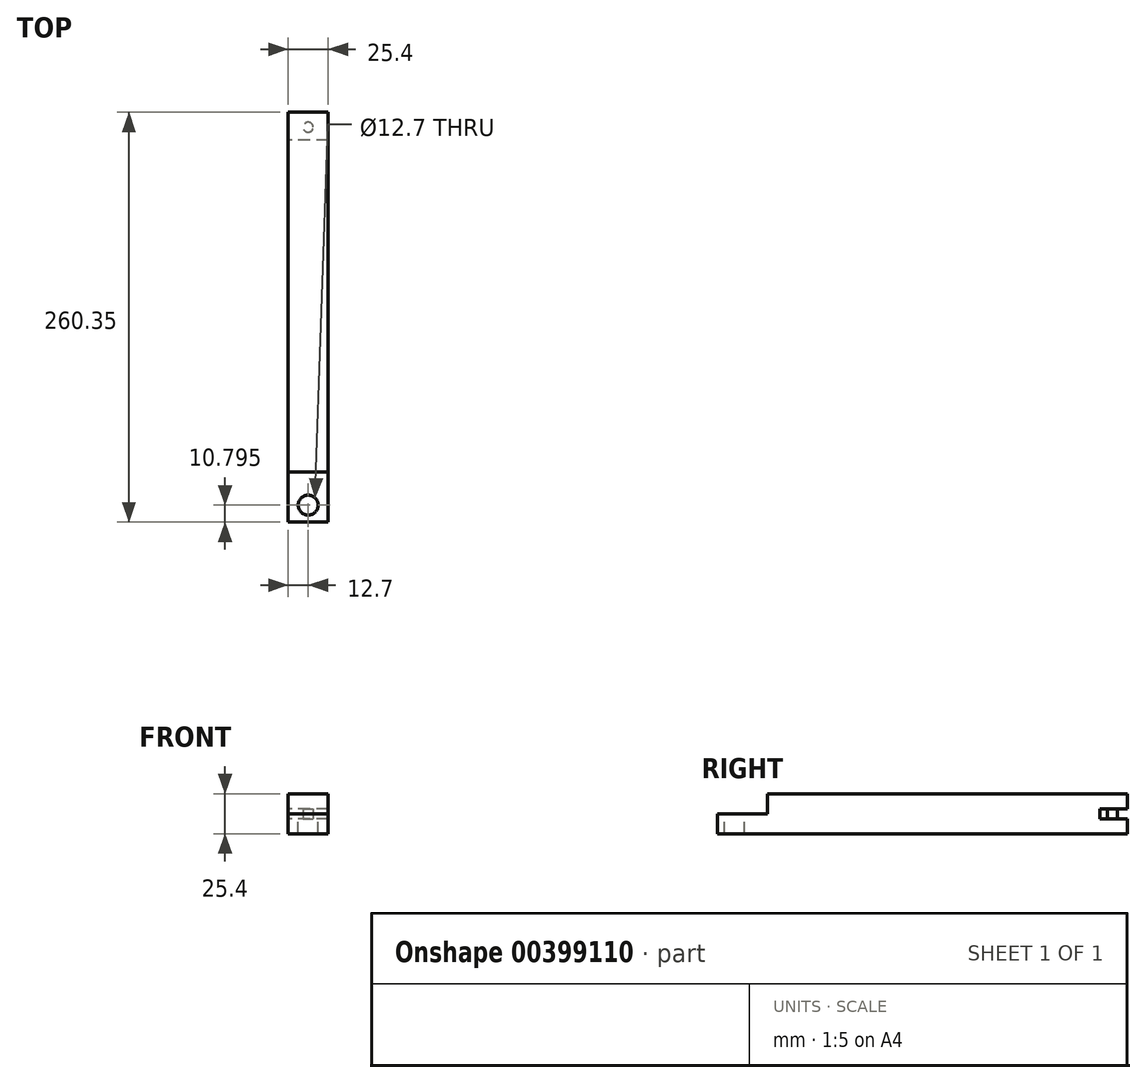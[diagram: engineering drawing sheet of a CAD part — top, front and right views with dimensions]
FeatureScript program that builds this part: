
annotation { "Feature Type Name" : "Feature", "Feature Type Description" : "" }
export const myFeature = defineFeature(function(context is Context, id is Id, definition is map)
    precondition{}
    {
        {
            var Q0;
            Q0=qCreatedBy(makeId("Right.planeOp"),FACE);
            var sketch = newSketch(context, id + "F0", { "sketchPlane" : qUnion([Q0])});
            skLineSegment(sketch, "E0.bottom", {"start": v(0, 0) * mm, "end": v(260.35, 0) * mm});
            skLineSegment(sketch, "E0.top", {"start": v(0, 25.4) * mm, "end": v(260.35, 25.4) * mm});
            skLineSegment(sketch, "E0.left", {"start": v(0, 0) * mm, "end": v(0, 25.4) * mm});
            skLineSegment(sketch, "E0.right", {"start": v(260.35, 0) * mm, "end": v(260.35, 25.4) * mm});
            skLineSegment(sketch, "E1.bottom", {"start": v(260.35, 15.88) * mm, "end": v(242.71, 15.88) * mm});
            skLineSegment(sketch, "E1.top", {"start": v(260.35, 9.53) * mm, "end": v(242.71, 9.52) * mm});
            skLineSegment(sketch, "E1.left", {"start": v(260.35, 15.88) * mm, "end": v(260.35, 9.53) * mm});
            skLineSegment(sketch, "E1.right", {"start": v(242.71, 15.88) * mm, "end": v(242.71, 9.52) * mm});
            skSolve(sketch);
        }
        {
            var Q0;
            {var subQ1=sQuery(id+"F0.wireOp",EDGE,"E0.bottom");Q0=makeQuery(id+"F0.imprint","IMPRINT",FACE,{"disambiguationData":[TD([[makeQuery(id+"F0.imprint","IMPRINT",EDGE,{"derivedFrom":subQ1}),1.0]])]});}
            extrude(context, id + "F1", {"entities" : qUnion([Q0]), "depth" : 25.4 * mm});
        }
        {
            var Q0;
            Q0=makeQuery(id+"F1.opExtrude","CAP_FACE",FACE,{"disambiguationData":[OSD([sQuery(id+"F0.wireOp",EDGE,"E0.bottom"),sQuery(id+"F0.wireOp",EDGE,"E0.top"),sQuery(id+"F0.wireOp",EDGE,"E0.left"),sQuery(id+"F0.wireOp",EDGE,"E0.right"),sQuery(id+"F0.wireOp",EDGE,"E1.bottom"),sQuery(id+"F0.wireOp",EDGE,"E1.top"),sQuery(id+"F0.wireOp",EDGE,"E1.right")])],"isStart":false});
            var sketch = newSketch(context, id + "F2", { "sketchPlane" : qUnion([Q0])});
            skPoint(sketch, "E2.oppositeSnap0", {"position": v(0, 12.7) * mm});
            skLineSegment(sketch, "E2.bottom", {"start": v(0, 25.4) * mm, "end": v(31.75, 25.4) * mm});
            skLineSegment(sketch, "E2.top", {"start": v(0, 12.7) * mm, "end": v(31.75, 12.7) * mm});
            skLineSegment(sketch, "E2.left", {"start": v(0, 25.4) * mm, "end": v(0, 12.7) * mm});
            skLineSegment(sketch, "E2.right", {"start": v(31.75, 25.4) * mm, "end": v(31.75, 12.7) * mm});
            skSolve(sketch);
        }
        {
            var Q0;
            Q0=makeQuery(id+"F2.imprint","IMPRINT",FACE,{"disambiguationData":[TD([[makeQuery(id+"F2.imprint","IMPRINT",EDGE,{"derivedFrom":sQuery(id+"F2.wireOp",EDGE,"E2.bottom")}),-1.0]])]});
            extrude(context, id + "F3", {"entities" : qUnion([Q0]), "operationType" : NewBodyOperationType.REMOVE, "oppositeDirection" : true, "depth" : 25.4 * mm});
        }
        {
            var Q0;
            Q0=makeQuery(id+"F1.opExtrude","SWEPT_FACE",FACE,{"disambiguationData":[OSD([sQuery(id+"F0.wireOp",EDGE,"E0.bottom")])]});
            var sketch = newSketch(context, id + "F4", { "sketchPlane" : qUnion([Q0])});
            skCircle(sketch, "E3", {"center": v(12.7, -250.82) * mm, "radius": 3.18 * mm});
            skSolve(sketch);
        }
        {
            var Q0;
            Q0=makeQuery(id+"F4.imprint","IMPRINT",FACE,{"disambiguationData":[TD([[makeQuery(id+"F4.imprint","IMPRINT",EDGE,{"derivedFrom":sQuery(id+"F4.wireOp",EDGE,"E3")}),1.0]])]});
            extrude(context, id + "F5", {"entities" : qUnion([Q0]), "operationType" : NewBodyOperationType.ADD, "oppositeDirection" : true, "depth" : 25.4 * mm});
        }
        {
            var Q0;
            Q0=makeQuery(id+"F3.boolean.opBoolean","COPY",FACE,{"derivedFrom":makeQuery(id+"F3.opExtrude","SWEPT_FACE",FACE,{"disambiguationData":[OSD([sQuery(id+"F2.wireOp",EDGE,"E2.top")])]})});
            var sketch = newSketch(context, id + "F6", { "sketchPlane" : qUnion([Q0])});
            skCircle(sketch, "E4", {"center": v(12.7, 10.8) * mm, "radius": 6.35 * mm});
            skSolve(sketch);
        }
        {
            var Q0;
            Q0=makeQuery(id+"F6.imprint","IMPRINT",FACE,{"disambiguationData":[TD([[makeQuery(id+"F6.imprint","IMPRINT",EDGE,{"derivedFrom":sQuery(id+"F6.wireOp",EDGE,"E4")}),1.0]])]});
            extrude(context, id + "F7", {"entities" : qUnion([Q0]), "operationType" : NewBodyOperationType.REMOVE, "oppositeDirection" : true, "depth" : 25.4 * mm});
        }
    });
